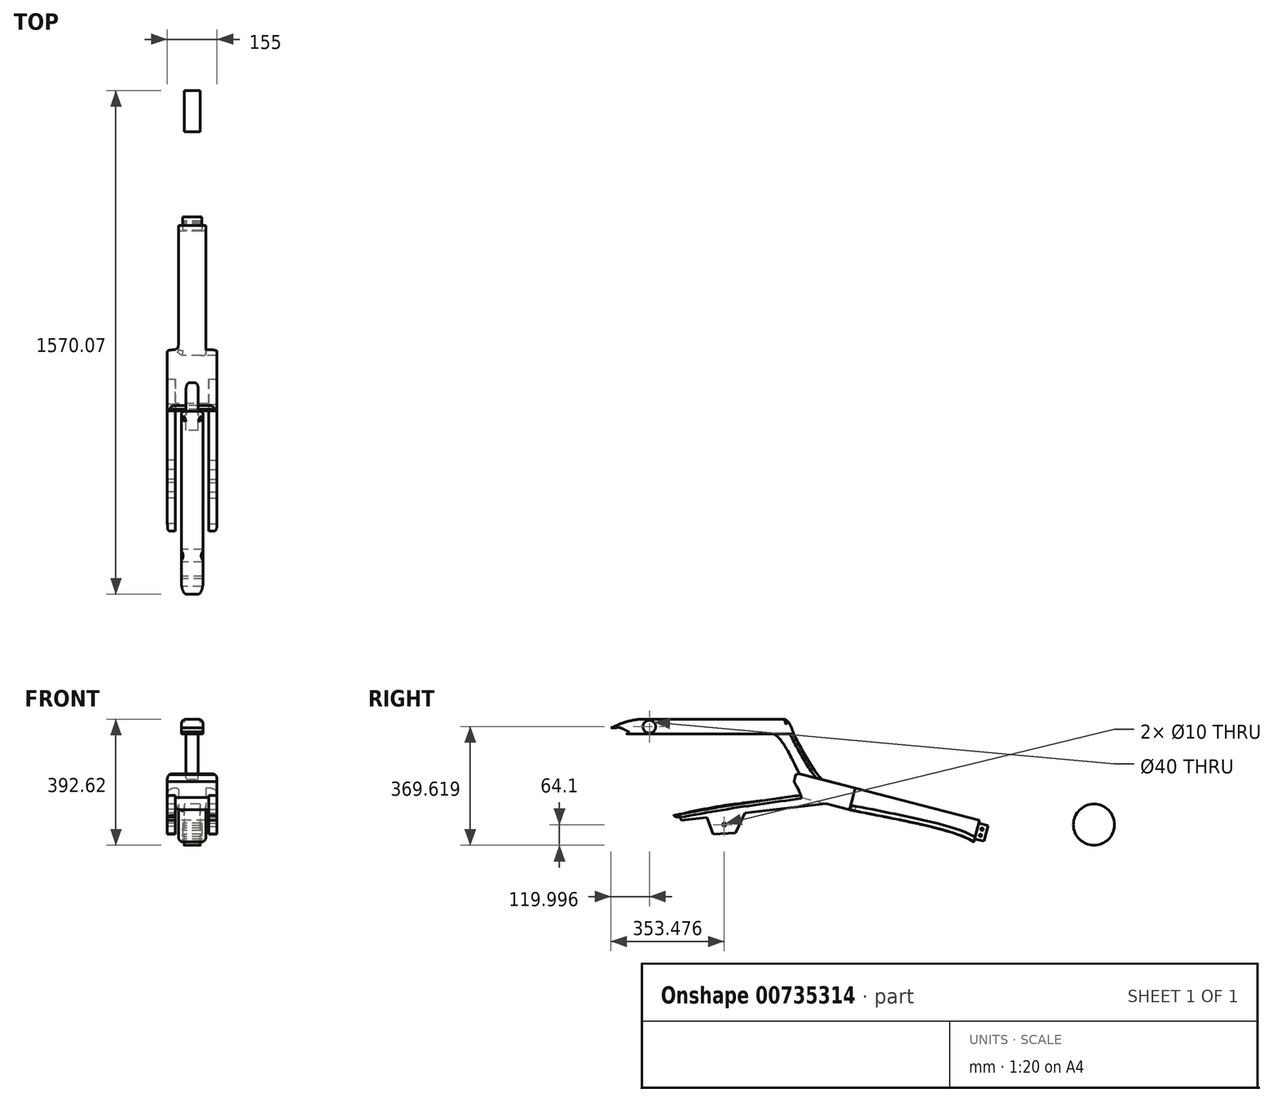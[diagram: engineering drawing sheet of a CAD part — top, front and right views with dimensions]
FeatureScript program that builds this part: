
annotation { "Feature Type Name" : "Feature", "Feature Type Description" : "" }
export const myFeature = defineFeature(function(context is Context, id is Id, definition is map)
    precondition{}
    {
        {
            var Q0;
            Q0=qCreatedBy(makeId("Right.planeOp"),FACE);
            var sketch = newSketch(context, id + "F0", { "sketchPlane" : qUnion([Q0])});
            skLineSegment(sketch, "E0", {"start": v(-839.21, 0) * mm, "end": v(-890, 0) * mm, "construction": true});
            skLineSegment(sketch, "E1", {"start": v(-890, 0) * mm, "end": v(-890, 230) * mm, "construction": true});
            skLineSegment(sketch, "E2", {"start": v(-890, 230) * mm, "end": v(0, 0) * mm, "construction": true});
            skCircle(sketch, "E3", {"center": v(-636.21, 0) * mm, "radius": 203 * mm});
            skCircle(sketch, "E4", {"center": v(513.79, 0) * mm, "radius": 203 * mm});
            skLineSegment(sketch, "E5.bottom", {"start": v(-636.21, 0) * mm, "end": v(513.79, 0) * mm, "construction": true});
            skLineSegment(sketch, "E6", {"start": v(-839.21, 0) * mm, "end": v(-636.21, 0) * mm, "construction": true});
            skCircle(sketch, "E7.0", {"center": v(-636.21, 0) * mm, "radius": 248 * mm});
            skCircle(sketch, "E8.0", {"center": v(513.79, 0) * mm, "radius": 248 * mm});
            skLineSegment(sketch, "E9", {"start": v(0, 0) * mm, "end": v(19.52, 75.52) * mm, "construction": true});
            skLineSegment(sketch, "E10", {"start": v(19.52, 75.52) * mm, "end": v(-870.48, 305.52) * mm, "construction": true});
            skLineSegment(sketch, "E11", {"start": v(-870.48, 305.52) * mm, "end": v(-890, 230) * mm, "construction": true});
            skCircle(sketch, "E12", {"center": v(-870.48, 305.52) * mm, "radius": 22.5 * mm});
            skCircle(sketch, "E13", {"center": v(-870.48, 305.52) * mm, "radius": 21 * mm});
            skCircle(sketch, "E14", {"center": v(-870.48, 305.52) * mm, "radius": 110 * mm});
            skLineSegment(sketch, "E15", {"start": v(19.52, 75.52) * mm, "end": v(573.04, 539.98) * mm, "construction": true});
            skLineSegment(sketch, "E16", {"start": v(-86.27, 75.52) * mm, "end": v(113.73, 75.52) * mm, "construction": true});
            skLineSegment(sketch, "E17", {"start": v(-636.21, 0) * mm, "end": v(-636.21, -248) * mm, "construction": true});
            skLineSegment(sketch, "E18", {"start": v(-636.21, -248) * mm, "end": v(513.79, -248) * mm, "construction": true});
            skLineSegment(sketch, "E19", {"start": v(513.79, -248) * mm, "end": v(513.79, 0) * mm, "construction": true});
            skSolve(sketch);
        }
        {
            var Q0;
            Q0=qCreatedBy(makeId("Right.planeOp"),FACE);
            cPlane(context, id + "F1", {"entities" : qUnion([Q0]), "cplaneType" : CPlaneType.OFFSET, "offset" : 65 * mm, "oppositeDirection" : true, "width" : 150 * mm, "height" : 150 * mm});
        }
        {
            var Q0;
            Q0=qCreatedBy(makeId("Right.planeOp"),FACE);
            cPlane(context, id + "F2", {"entities" : qUnion([Q0]), "cplaneType" : CPlaneType.OFFSET, "offset" : 65 * mm, "width" : 150 * mm, "height" : 150 * mm});
        }
        {
            var Q0;
            Q0=qCreatedBy(makeId("Right.planeOp"),FACE);
            var sketch = newSketch(context, id + "F3", { "sketchPlane" : qUnion([Q0])});
            skLineSegment(sketch, "E20", {"start": v(-228.79, 113.87) * mm, "end": v(158.49, 13.78) * mm});
            skLineSegment(sketch, "E21.bottom", {"start": v(-990.48, 328.52) * mm, "end": v(-420.48, 328.52) * mm, "construction": true});
            skLineSegment(sketch, "E21.top", {"start": v(-990.48, 282.52) * mm, "end": v(-420.48, 282.52) * mm, "construction": true});
            skLineSegment(sketch, "E21.left", {"start": v(-990.48, 328.52) * mm, "end": v(-990.48, 282.52) * mm, "construction": true});
            skLineSegment(sketch, "E21.right", {"start": v(-420.48, 328.52) * mm, "end": v(-420.48, 282.52) * mm, "construction": true});
            skLineSegment(sketch, "E22", {"start": v(-228.79, 113.87) * mm, "end": v(-403.06, 158.9) * mm});
            skLineSegment(sketch, "E23", {"start": v(-412.74, 161.4) * mm, "end": v(-430.26, 93.63) * mm, "construction": true});
            skLineSegment(sketch, "E24", {"start": v(-430.26, 93.63) * mm, "end": v(-246.3, 46.1) * mm, "construction": true});
            skLineSegment(sketch, "E25", {"start": v(158.49, 13.78) * mm, "end": v(140.98, -54) * mm});
            skLineSegment(sketch, "E26", {"start": v(-228.79, 113.87) * mm, "end": v(-246.3, 46.1) * mm});
            skLineSegment(sketch, "E27", {"start": v(-990.48, 305.52) * mm, "end": v(-420.48, 305.52) * mm, "construction": true});
            skLineSegment(sketch, "E28", {"start": v(-420.48, 282.52) * mm, "end": v(-331.58, 140.43) * mm, "construction": true});
            skLineSegment(sketch, "E29", {"start": v(-480.4, 282.52) * mm, "end": v(-403.06, 158.9) * mm, "construction": true});
            skCircle(sketch, "E30", {"center": v(-870.48, 305.52) * mm, "radius": 20 * mm});
            skFitSpline(sketch, "E31", {"points": [v(-446.93, 328.52) * mm, v(-420.48, 282.52) * mm], "startDerivative": vector(40.95, -24.88) * mm, "endDerivative": vector(18.36, -59.68) * mm});
            skLineSegment(sketch, "E32", {"start": v(-480.4, 282.52) * mm, "end": v(-420.48, 282.52) * mm});
            skFitSpline(sketch, "E33", {"points": [v(-480.4, 282.52) * mm, v(-403.06, 158.9) * mm], "startDerivative": vector(83.68, -66.51) * mm, "endDerivative": vector(113.52, -228.08) * mm});
            skFitSpline(sketch, "E34", {"points": [v(-420.48, 282.52) * mm, v(-331.58, 140.43) * mm], "startDerivative": vector(46.18, -95.07) * mm, "endDerivative": vector(81.7, -70.02) * mm});
            skLineSegment(sketch, "E35", {"start": v(-396.57, 84.92) * mm, "end": v(-246.3, 46.1) * mm});
            skFitSpline(sketch, "E36", {"points": [v(-419.66, 134.65) * mm, v(-396.57, 84.92) * mm], "startDerivative": vector(31.98, -52.88) * mm, "endDerivative": vector(7.26, -32.36) * mm});
            skFitSpline(sketch, "E37", {"points": [v(-403.06, 158.9) * mm, v(-414.1, 156.15) * mm], "startDerivative": vector(-13.37, -1.9) * mm, "endDerivative": vector(-11.19, -2.08) * mm});
            skFitSpline(sketch, "E38", {"points": [v(-414.1, 156.15) * mm, v(-419.66, 134.65) * mm], "startDerivative": vector(-4.9, -18.97) * mm, "endDerivative": vector(0.06, 8.38) * mm});
            skLineSegment(sketch, "E39", {"start": v(-430.26, 93.63) * mm, "end": v(140.98, -54) * mm, "construction": true});
            skFitSpline(sketch, "E40", {"points": [v(-246.3, 46.1) * mm, v(140.98, -54) * mm], "startDerivative": vector(593.3, -116.1) * mm, "endDerivative": vector(155.05, -104.97) * mm});
            skCircle(sketch, "E41", {"center": v(166.76, -14.17) * mm, "radius": 4 * mm});
            skCircle(sketch, "E42", {"center": v(161.75, -33.54) * mm, "radius": 4 * mm});
            skLineSegment(sketch, "E43", {"start": v(-900.48, 328.52) * mm, "end": v(-870.48, 305.52) * mm, "construction": true});
            skFitSpline(sketch, "E44", {"points": [v(-900.48, 328.52) * mm, v(-990.48, 301.22) * mm], "startDerivative": vector(-118.47, -11.59) * mm, "endDerivative": vector(-75.39, -34.72) * mm});
            skLineSegment(sketch, "E45", {"start": v(-900.48, 328.52) * mm, "end": v(-446.93, 328.52) * mm});
            skLineSegment(sketch, "E46", {"start": v(-420.48, 282.52) * mm, "end": v(-941.99, 282.52) * mm});
            skFitSpline(sketch, "E47", {"points": [v(-990.48, 301.22) * mm, v(-966.17, 303.05) * mm], "startDerivative": vector(15.61, 2.31) * mm, "endDerivative": vector(15.61, 2.31) * mm});
            skFitSpline(sketch, "E48", {"points": [v(-966.17, 303.05) * mm, v(-934.37, 289.04) * mm], "startDerivative": vector(29.52, -2.6) * mm, "endDerivative": vector(28.82, -13.66) * mm});
            skFitSpline(sketch, "E49", {"points": [v(-934.37, 289.04) * mm, v(-941.99, 282.52) * mm], "startDerivative": vector(-7.1, -7.67) * mm, "endDerivative": vector(-7.31, -5.1) * mm});
            skLineSegment(sketch, "E50", {"start": v(-480.4, 282.52) * mm, "end": v(-361.43, 356.97) * mm, "construction": true});
            skLineSegment(sketch, "E51", {"start": v(-331.58, 140.43) * mm, "end": v(-237.61, 199.22) * mm, "construction": true});
            skLineSegment(sketch, "E52", {"start": v(155.99, 4.1) * mm, "end": v(185.03, -3.4) * mm});
            skLineSegment(sketch, "E53", {"start": v(185.03, -3.4) * mm, "end": v(172.52, -51.81) * mm});
            skLineSegment(sketch, "E54", {"start": v(172.52, -51.81) * mm, "end": v(143.48, -44.3) * mm});
            skLineSegment(sketch, "E55", {"start": v(170.51, 0.35) * mm, "end": v(158, -48.06) * mm, "construction": true});
            skSolve(sketch);
        }
        {
            var Q0;
            Q0=makeQuery(id+"F3.imprint","IMPRINT",FACE,{"disambiguationData":[TD([[makeQuery(id+"F3.imprint","IMPRINT",EDGE,{"derivedFrom":sQuery(id+"F3.wireOp",EDGE,"E30")}),-1.0]])]});
            extrude(context, id + "F4", {"entities" : qUnion([Q0]), "endBound" : BoundingType.SYMMETRIC, "depth" : 68 * mm, "offsetDistance" : 25 * mm});
        }
        {
            var Q0;
            Q0=makeQuery(id+"F3.imprint","IMPRINT",FACE,{"disambiguationData":[TD([[makeQuery(id+"F3.imprint","IMPRINT",EDGE,{"derivedFrom":sQuery(id+"F3.wireOp",EDGE,"E32")}),-1.0]])]});
            extrude(context, id + "F5", {"entities" : qUnion([Q0]), "operationType" : NewBodyOperationType.ADD, "endBound" : BoundingType.SYMMETRIC, "depth" : 38.1 * mm, "offsetDistance" : 25 * mm});
        }
        {
            var Q0;
            {var subQ1=sQuery(id+"F3.wireOp",EDGE,"E26");Q0=makeQuery(id+"F3.imprint","IMPRINT",FACE,{"disambiguationData":[TD([[makeQuery(id+"F3.imprint","IMPRINT",EDGE,{"derivedFrom":subQ1}),-1.0]])]});}
            extrude(context, id + "F6", {"entities" : qUnion([Q0]), "operationType" : NewBodyOperationType.ADD, "endBound" : BoundingType.SYMMETRIC, "depth" : 155 * mm, "offsetDistance" : 25 * mm});
        }
        {
            var Q0;
            Q0=makeQuery(id+"F6.opExtrude","CAP_FACE",FACE,{"disambiguationData":[OSD([sQuery(id+"F3.wireOp",EDGE,"E22"),sQuery(id+"F3.wireOp",EDGE,"E26"),sQuery(id+"F3.wireOp",EDGE,"E35"),sQuery(id+"F3.wireOp",EDGE,"E36"),sQuery(id+"F3.wireOp",EDGE,"E37"),sQuery(id+"F3.wireOp",EDGE,"E38")])],"isStart":false});
            var sketch = newSketch(context, id + "F7", { "sketchPlane" : qUnion([Q0])});
            skLineSegment(sketch, "E56", {"start": v(-304.09, 102.34) * mm, "end": v(-257.8, 93.53) * mm, "construction": true});
            skLineSegment(sketch, "E57", {"start": v(-257.8, 93.53) * mm, "end": v(-255.41, 72.67) * mm, "construction": true});
            skLineSegment(sketch, "E58", {"start": v(-255.41, 72.67) * mm, "end": v(-791.93, 11.44) * mm, "construction": true});
            skLineSegment(sketch, "E59", {"start": v(-791.93, 11.44) * mm, "end": v(-795.9, 46.22) * mm, "construction": true});
            skLineSegment(sketch, "E60", {"start": v(-795.9, 46.22) * mm, "end": v(-304.09, 102.34) * mm, "construction": true});
            skLineSegment(sketch, "E61", {"start": v(-573.32, 36.39) * mm, "end": v(-601.7, -25.77) * mm});
            skLineSegment(sketch, "E62", {"start": v(-601.7, -25.77) * mm, "end": v(-672.4, -29.77) * mm});
            skLineSegment(sketch, "E63", {"start": v(-672.4, -29.77) * mm, "end": v(-691.03, 22.96) * mm});
            skCircle(sketch, "E64", {"center": v(-637, 0) * mm, "radius": 5 * mm});
            skPoint(sketch, "E65", {"position": v(-320.43, 65.25) * mm});
            skLineSegment(sketch, "E66", {"start": v(-255.41, 72.67) * mm, "end": v(-771.24, 13.8) * mm});
            skFitSpline(sketch, "E67", {"points": [v(-771.24, 13.8) * mm, v(-793.91, 28.83) * mm], "startDerivative": vector(-11.51, 40.5) * mm, "endDerivative": vector(-30.67, 16.33) * mm});
            skLineSegment(sketch, "E68", {"start": v(-304.09, 102.34) * mm, "end": v(-398.53, 91.56) * mm});
            skLineSegment(sketch, "E69", {"start": v(-304.09, 102.34) * mm, "end": v(-257.8, 93.53) * mm});
            skLineSegment(sketch, "E70", {"start": v(-255.41, 72.67) * mm, "end": v(-257.8, 93.53) * mm});
            skFitSpline(sketch, "E71", {"points": [v(-398.53, 91.56) * mm, v(-793.91, 28.83) * mm], "startDerivative": vector(-396.31, -54.62) * mm, "endDerivative": vector(-425.7, -85.53) * mm});
            skSolve(sketch);
        }
        {
            var Q0;
            {var subQ1=sQuery(id+"F3.wireOp",EDGE,"E20");Q0=makeQuery(id+"F3.imprint","IMPRINT",FACE,{"disambiguationData":[TD([[makeQuery(id+"F3.imprint","IMPRINT",EDGE,{"derivedFrom":subQ1}),-1.0]])]});}
            extrude(context, id + "F8", {"entities" : qUnion([Q0]), "operationType" : NewBodyOperationType.ADD, "endBound" : BoundingType.SYMMETRIC, "depth" : 86 * mm, "offsetDistance" : 25 * mm});
        }
        {
            var Q0;
            Q0=makeQuery(id+"F6.opExtrude","CAP_FACE",FACE,{"disambiguationData":[OSD([sQuery(id+"F3.wireOp",EDGE,"E22"),sQuery(id+"F3.wireOp",EDGE,"E26"),sQuery(id+"F3.wireOp",EDGE,"E35"),sQuery(id+"F3.wireOp",EDGE,"E36"),sQuery(id+"F3.wireOp",EDGE,"E37"),sQuery(id+"F3.wireOp",EDGE,"E38")])],"isStart":true});
            var sketch = newSketch(context, id + "F9", { "sketchPlane" : qUnion([Q0])});
            skLineSegment(sketch, "E72.0.0", {"start": v(573.32, 36.39) * mm, "end": v(320.43, 65.25) * mm});
            skLineSegment(sketch, "E72.0.1", {"start": v(320.43, 65.25) * mm, "end": v(396.57, 84.92) * mm});
            skFitSpline(sketch, "E72.0.2", {"points": [v(396.57, 84.92) * mm, v(398.98, 95.71) * mm, v(409, 117.02) * mm, v(419.66, 134.65) * mm]});
            skFitSpline(sketch, "E72.0.3", {"points": [v(398.53, 91.56) * mm, v(530.63, 73.36) * mm, v(652.01, 57.34) * mm, v(793.91, 28.83) * mm]});
            skFitSpline(sketch, "E72.0.4", {"points": [v(793.91, 28.83) * mm, v(783.7, 23.39) * mm, v(775.08, 27.3) * mm, v(771.24, 13.8) * mm]});
            skLineSegment(sketch, "E72.0.5", {"start": v(771.24, 13.8) * mm, "end": v(691.03, 22.96) * mm});
            skLineSegment(sketch, "E72.0.6", {"start": v(691.03, 22.96) * mm, "end": v(573.32, 36.39) * mm});
            skLineSegment(sketch, "E73.0.0", {"start": v(601.7, -25.77) * mm, "end": v(573.32, 36.39) * mm});
            skLineSegment(sketch, "E73.0.1", {"start": v(573.32, 36.39) * mm, "end": v(691.03, 22.96) * mm});
            skLineSegment(sketch, "E73.0.2", {"start": v(691.03, 22.96) * mm, "end": v(672.4, -29.77) * mm});
            skLineSegment(sketch, "E73.0.3", {"start": v(672.4, -29.77) * mm, "end": v(601.7, -25.77) * mm});
            skCircle(sketch, "E74.0", {"center": v(637, 0) * mm, "radius": 5 * mm});
            skLineSegment(sketch, "E75.0.0", {"start": v(257.8, 93.53) * mm, "end": v(304.09, 102.34) * mm});
            skLineSegment(sketch, "E75.0.1", {"start": v(304.09, 102.34) * mm, "end": v(398.53, 91.56) * mm});
            skFitSpline(sketch, "E75.0.2", {"points": [v(419.66, 134.65) * mm, v(409, 117.02) * mm, v(398.98, 95.71) * mm, v(396.57, 84.92) * mm]});
            skLineSegment(sketch, "E75.0.3", {"start": v(396.57, 84.92) * mm, "end": v(320.43, 65.25) * mm});
            skLineSegment(sketch, "E75.0.4", {"start": v(320.43, 65.25) * mm, "end": v(255.41, 72.67) * mm});
            skLineSegment(sketch, "E75.0.5", {"start": v(255.41, 72.67) * mm, "end": v(257.8, 93.53) * mm});
            skSolve(sketch);
        }
        {
            var Q0;
            Q0=makeQuery(id+"F3.imprint","IMPRINT",FACE,{"disambiguationData":[TD([[makeQuery(id+"F3.imprint","IMPRINT",EDGE,{"derivedFrom":sQuery(id+"F3.wireOp",EDGE,"E41")}),-1.0]])]});
            extrude(context, id + "F10", {"entities" : qUnion([Q0]), "operationType" : NewBodyOperationType.ADD, "endBound" : BoundingType.SYMMETRIC, "depth" : 60 * mm, "offsetDistance" : 25 * mm});
        }
        {
            var Q0;
            {var subQ0=sQuery(id+"F7.wireOp",EDGE,"E67");Q0=makeQuery(id+"F7.imprint","IMPRINT",FACE,{"disambiguationData":[TD([[makeQuery(id+"F7.imprint","IMPRINT",EDGE,{"derivedFrom":subQ0}),-1.0]])]});}
            var Q1;
            {var subQ1=sQuery(id+"F7.wireOp",EDGE,"E61");Q1=makeQuery(id+"F7.imprint","IMPRINT",FACE,{"disambiguationData":[TD([[makeQuery(id+"F7.imprint","IMPRINT",EDGE,{"derivedFrom":subQ1}),-1.0]])]});}
            var Q2;
            {var subQ1=sQuery(id+"F7.wireOp",EDGE,"E68");Q2=makeQuery(id+"F7.imprint","IMPRINT",FACE,{"disambiguationData":[TD([[makeQuery(id+"F7.imprint","IMPRINT",EDGE,{"derivedFrom":subQ1}),1.0]])]});}
            extrude(context, id + "F11", {"entities" : qUnion([Q0, Q1, Q2]), "operationType" : NewBodyOperationType.ADD, "oppositeDirection" : true, "depth" : 25.4 * mm, "offsetDistance" : 25 * mm});
        }
        {
            var Q0;
            Q0=makeQuery(id+"F8.opExtrude","CAP_EDGE",EDGE,{"disambiguationData":[OSD([sQuery(id+"F3.wireOp",EDGE,"E26")])],"isStart":true});
            var Q1;
            Q1=makeQuery(id+"F8.opExtrude","CAP_EDGE",EDGE,{"disambiguationData":[OSD([sQuery(id+"F3.wireOp",EDGE,"E26")])],"isStart":false});
            var Q2;
            Q2=makeQuery(id+"F4.opExtrude","CAP_EDGE",EDGE,{"disambiguationData":[OSD([sQuery(id+"F3.wireOp",EDGE,"E45")])],"isStart":false});
            var Q3;
            Q3=makeQuery(id+"F4.opExtrude","CAP_EDGE",EDGE,{"disambiguationData":[OSD([sQuery(id+"F3.wireOp",EDGE,"E45")])],"isStart":true});
            var Q4;
            Q4=makeQuery(id+"F4.opExtrude","CAP_EDGE",EDGE,{"disambiguationData":[OSD([sQuery(id+"F3.wireOp",EDGE,"E44")])],"isStart":false});
            var Q5;
            Q5=makeQuery(id+"F4.opExtrude","CAP_EDGE",EDGE,{"disambiguationData":[OSD([sQuery(id+"F3.wireOp",EDGE,"E44")])],"isStart":true});
            var Q6;
            Q6=makeQuery(id+"F4.opExtrude","SWEPT_EDGE",EDGE,{"disambiguationData":[OSD([sQuery(id+"F3.wireOp",EDGE,"E31"),sQuery(id+"F3.wireOp",EDGE,"E45")])]});
            var Q7;
            Q7=makeQuery(id+"F4.opExtrude","SWEPT_EDGE",EDGE,{"disambiguationData":[OSD([sQuery(id+"F3.wireOp",EDGE,"E44"),sQuery(id+"F3.wireOp",EDGE,"E45")])]});
            fillet(context, id + "F12", {"entities" : qUnion([Q0, Q1, Q2, Q3, Q4, Q5, Q6, Q7]), "radius" : 15 * mm, "tangentPropagation" : true, "allowEdgeOverflow" : false});
        }
        {
            var Q0;
            Q0=makeQuery(id+"F5.opExtrude","CAP_EDGE",EDGE,{"disambiguationData":[OSD([sQuery(id+"F3.wireOp",EDGE,"E34")])],"isStart":false});
            var Q1;
            Q1=makeQuery(id+"F5.opExtrude","CAP_EDGE",EDGE,{"disambiguationData":[OSD([sQuery(id+"F3.wireOp",EDGE,"E34")])],"isStart":true});
            var Q2;
            Q2=makeQuery(id+"F11.opExtrude","CAP_EDGE",EDGE,{"disambiguationData":[OSD([sQuery(id+"F7.wireOp",EDGE,"2d2ba40c-a02e-4269-819a-9c400366be13")])],"isStart":true});
            var Q3;
            Q3=makeQuery(id+"FFKQbZDGYRM2YjH_1.opExtrude","CAP_EDGE",EDGE,{"disambiguationData":[OSD([sQuery(id+"F9.wireOp",EDGE,"418496da-3a12-4d16-a20d-26360628b4ec.2")])],"isStart":true});
            var Q4;
            Q4=makeQuery(id+"F4.opExtrude","CAP_EDGE",EDGE,{"disambiguationData":[OSD([sQuery(id+"F3.wireOp",EDGE,"E31")])],"isStart":false});
            var Q5;
            Q5=makeQuery(id+"F4.opExtrude","CAP_EDGE",EDGE,{"disambiguationData":[OSD([sQuery(id+"F3.wireOp",EDGE,"E31")])],"isStart":true});
            fillet(context, id + "F13", {"entities" : qUnion([Q0, Q1, Q2, Q3, Q4, Q5]), "radius" : 10 * mm, "tangentPropagation" : true, "allowEdgeOverflow" : false});
        }
        {
            var Q0;
            Q0=makeQuery(id+"F4.opExtrude","CAP_EDGE",EDGE,{"disambiguationData":[OSD([sQuery(id+"F3.wireOp",EDGE,"81e0ebba-2043-46d8-adfa-aa85b01486f9")])],"isStart":true});
            var Q1;
            Q1=makeQuery(id+"F4.opExtrude","CAP_EDGE",EDGE,{"disambiguationData":[OSD([sQuery(id+"F3.wireOp",EDGE,"81e0ebba-2043-46d8-adfa-aa85b01486f9")])],"isStart":false});
            var Q2;
            Q2=makeQuery(id+"F6.opExtrude","CAP_EDGE",EDGE,{"disambiguationData":[OSD([sQuery(id+"F3.wireOp",EDGE,"E22")])],"isStart":false});
            var Q3;
            Q3=makeQuery(id+"F6.opExtrude","CAP_EDGE",EDGE,{"disambiguationData":[OSD([sQuery(id+"F3.wireOp",EDGE,"E22")])],"isStart":true});
            fillet(context, id + "F14", {"entities" : qUnion([Q0, Q1, Q2, Q3]), "radius" : 20 * mm, "tangentPropagation" : true, "allowEdgeOverflow" : false});
        }
        {
            var Q0;
            Q0=makeQuery(id+"F8.opExtrude","CAP_EDGE",EDGE,{"disambiguationData":[OSD([sQuery(id+"F3.wireOp",EDGE,"E40")])],"isStart":false});
            var Q1;
            Q1=makeQuery(id+"F8.opExtrude","CAP_EDGE",EDGE,{"disambiguationData":[OSD([sQuery(id+"F3.wireOp",EDGE,"E40")])],"isStart":true});
            fillet(context, id + "F15", {"entities" : qUnion([Q0, Q1]), "radius" : 15 * mm, "tangentPropagation" : true, "allowEdgeOverflow" : false});
        }
        {
            var Q0;
            Q0=makeQuery(id+"F9.imprint","IMPRINT",FACE,{"disambiguationData":[TD([[makeQuery(id+"F9.imprint","IMPRINT",EDGE,{"derivedFrom":sQuery(id+"F9.wireOp",EDGE,"E72.0.0")}),-1.0]])]});
            var Q1;
            Q1=makeQuery(id+"F9.imprint","IMPRINT",FACE,{"disambiguationData":[TD([[makeQuery(id+"F9.imprint","IMPRINT",EDGE,{"derivedFrom":sQuery(id+"F9.wireOp",EDGE,"E75.0.0")}),-1.0]])]});
            var Q2;
            Q2=makeQuery(id+"F9.imprint","IMPRINT",FACE,{"disambiguationData":[TD([[makeQuery(id+"F9.imprint","IMPRINT",EDGE,{"derivedFrom":sQuery(id+"F9.wireOp",EDGE,"E73.0.0")}),-1.0]])]});
            extrude(context, id + "F16", {"entities" : qUnion([Q0, Q1, Q2]), "operationType" : NewBodyOperationType.ADD, "oppositeDirection" : true, "depth" : 25 * mm, "offsetDistance" : 25 * mm});
        }
        {
            var Q0;
            Q0=makeQuery(id+"F16.opExtrude","CAP_EDGE",EDGE,{"disambiguationData":[OSD([sQuery(id+"F9.wireOp",EDGE,"E72.0.3")])],"isStart":true});
            var Q1;
            Q1=makeQuery(id+"F11.opExtrude","CAP_EDGE",EDGE,{"disambiguationData":[OSD([sQuery(id+"F7.wireOp",EDGE,"E71")])],"isStart":true});
            fillet(context, id + "F17", {"entities" : qUnion([Q0, Q1]), "radius" : 10 * mm, "tangentPropagation" : true, "allowEdgeOverflow" : false});
        }
        {
            var Q0;
            Q0=makeQuery(id+"F0.imprint","IMPRINT",FACE,{"disambiguationData":[TD([[makeQuery(id+"F0.imprint","IMPRINT",EDGE,{"derivedFrom":sQuery(id+"F0.wireOp",EDGE,"E4")}),1.0]])]});
            var sketch = newSketch(context, id + "F18", { "sketchPlane" : qUnion([Q0])});
            skCircle(sketch, "E76", {"center": v(515.5, 0) * mm, "radius": 64.1 * mm});
            skSolve(sketch);
        }
        {
            var Q0;
            Q0 = qSketchRegion(id + "F18", true);
            extrude(context, id + "F19", {"entities" : qUnion([Q0]), "depth" : 25 * mm, "offsetDistance" : 25 * mm, "hasSecondDirection" : true, "secondDirectionOppositeDirection" : true, "secondDirectionDepth" : 25 * mm});
        }
    });
